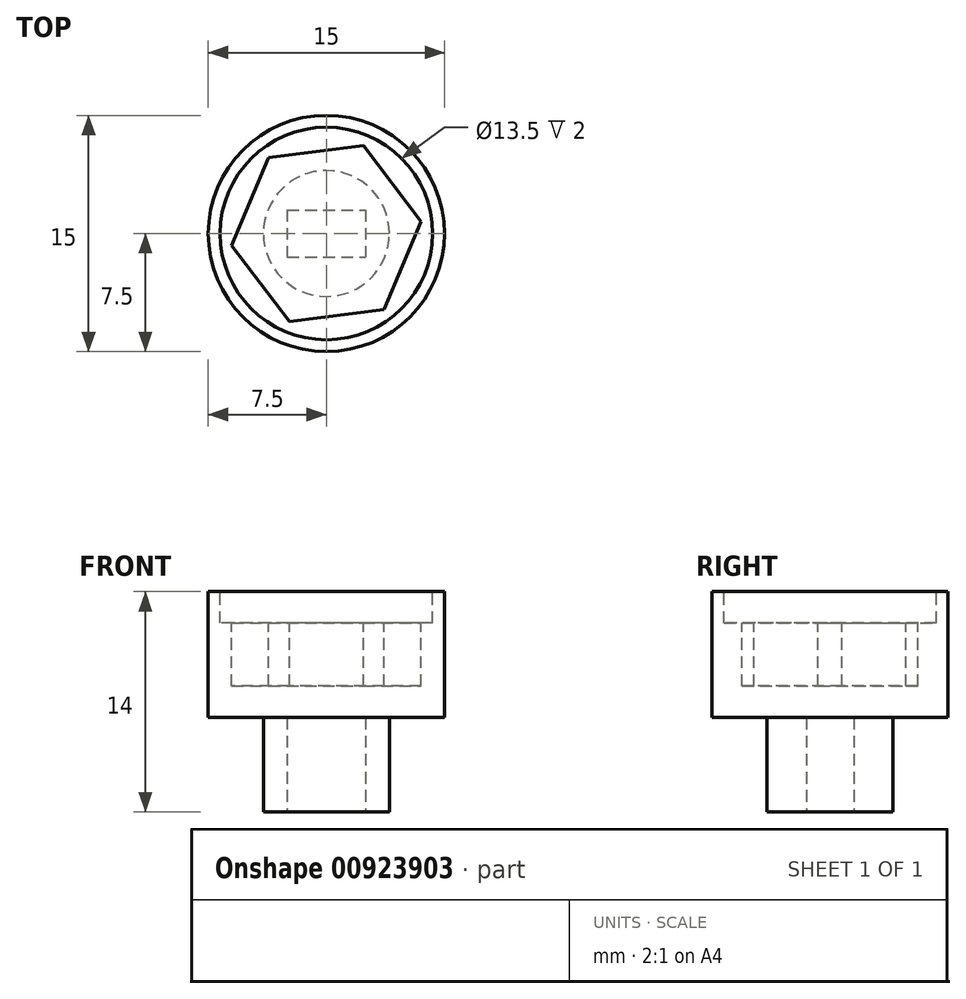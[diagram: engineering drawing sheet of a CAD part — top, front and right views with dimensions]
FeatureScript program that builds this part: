
annotation { "Feature Type Name" : "Feature", "Feature Type Description" : "" }
export const myFeature = defineFeature(function(context is Context, id is Id, definition is map)
    precondition{}
    {
        {
            var Q0;
            Q0=qCreatedBy(makeId("Top.planeOp"),FACE);
            var sketch = newSketch(context, id + "F0", { "sketchPlane" : qUnion([Q0])});
            skCircle(sketch, "E0", {"center": v(0, 0) * mm, "radius": 7.5 * mm});
            skSolve(sketch);
        }
        {
            var Q0;
            Q0 = qSketchRegion(id + "F0", true);
            extrude(context, id + "F1", {"entities" : qUnion([Q0]), "depth" : 8 * mm, "offsetDistance" : 25 * mm});
        }
        {
            var Q0;
            Q0=makeQuery(id+"F1.opExtrude","CAP_FACE",FACE,{"disambiguationData":[OSD([sQuery(id+"F0.wireOp",EDGE,"E0")])],"isStart":false});
            var sketch = newSketch(context, id + "F2", { "sketchPlane" : qUnion([Q0])});
            skCircle(sketch, "E1", {"center": v(0, 0) * mm, "radius": 6.75 * mm});
            skSolve(sketch);
        }
        {
            var Q0;
            Q0=makeQuery(id+"F2.imprint","IMPRINT",FACE,{"disambiguationData":[TD([[makeQuery(id+"F2.imprint","IMPRINT",EDGE,{"derivedFrom":sQuery(id+"F2.wireOp",EDGE,"E1")}),1.0]])]});
            extrude(context, id + "F3", {"entities" : qUnion([Q0]), "operationType" : NewBodyOperationType.REMOVE, "oppositeDirection" : true, "depth" : 2 * mm, "offsetDistance" : 25 * mm});
        }
        {
            var Q0;
            Q0=makeQuery(id+"F3.boolean.opBoolean","COPY",FACE,{"derivedFrom":makeQuery(id+"F3.opExtrude","CAP_FACE",FACE,{"disambiguationData":[OSD([sQuery(id+"F2.wireOp",EDGE,"E1")])],"isStart":false})});
            var sketch = newSketch(context, id + "F4", { "sketchPlane" : qUnion([Q0])});
            skCircle(sketch, "E2.cCircle", {"center": v(0, 0) * mm, "radius": 5.25 * mm, "construction": true});
            skLineSegment(sketch, "E2.0", {"start": v(2.34, 5.6) * mm, "end": v(6.01, 0.77) * mm});
            skLineSegment(sketch, "E2.1", {"start": v(6.01, 0.77) * mm, "end": v(3.67, -4.83) * mm});
            skLineSegment(sketch, "E2.2", {"start": v(3.67, -4.83) * mm, "end": v(-2.34, -5.6) * mm});
            skLineSegment(sketch, "E2.3", {"start": v(-2.34, -5.6) * mm, "end": v(-6.01, -0.77) * mm});
            skLineSegment(sketch, "E2.4", {"start": v(-6.01, -0.77) * mm, "end": v(-3.67, 4.83) * mm});
            skLineSegment(sketch, "E2.5", {"start": v(-3.67, 4.83) * mm, "end": v(2.34, 5.6) * mm});
            skPoint(sketch, "E2.0.midPoint", {"position": v(4.18, 3.18) * mm});
            skSolve(sketch);
        }
        {
            var Q0;
            Q0=makeQuery(id+"F4.imprint","IMPRINT",FACE,{"disambiguationData":[TD([[makeQuery(id+"F4.imprint","IMPRINT",EDGE,{"derivedFrom":sQuery(id+"F4.wireOp",EDGE,"E2.0")}),-1.0]])]});
            extrude(context, id + "F5", {"entities" : qUnion([Q0]), "operationType" : NewBodyOperationType.REMOVE, "oppositeDirection" : true, "depth" : 4 * mm, "offsetDistance" : 25 * mm});
        }
        {
            var Q0;
            Q0=makeQuery(id+"F1.opExtrude","CAP_FACE",FACE,{"disambiguationData":[OSD([sQuery(id+"F0.wireOp",EDGE,"E0")])],"isStart":true});
            var sketch = newSketch(context, id + "F6", { "sketchPlane" : qUnion([Q0])});
            skCircle(sketch, "E3", {"center": v(0, 0) * mm, "radius": 4 * mm});
            skSolve(sketch);
        }
        {
            var Q0;
            Q0=makeQuery(id+"F6.imprint","IMPRINT",FACE,{"disambiguationData":[TD([[makeQuery(id+"F6.imprint","IMPRINT",EDGE,{"derivedFrom":sQuery(id+"F6.wireOp",EDGE,"E3")}),1.0]])]});
            extrude(context, id + "F7", {"entities" : qUnion([Q0]), "operationType" : NewBodyOperationType.ADD, "depth" : 6 * mm, "offsetDistance" : 25 * mm});
        }
        {
            var Q0;
            Q0=makeQuery(id+"F7.opExtrude","CAP_FACE",FACE,{"disambiguationData":[OSD([sQuery(id+"F6.wireOp",EDGE,"E3")])],"isStart":false});
            var sketch = newSketch(context, id + "F8", { "sketchPlane" : qUnion([Q0])});
            skLineSegment(sketch, "E4.bottom", {"start": v(-2.5, -1.5) * mm, "end": v(2.5, -1.5) * mm});
            skLineSegment(sketch, "E4.top", {"start": v(-2.5, 1.5) * mm, "end": v(2.5, 1.5) * mm});
            skLineSegment(sketch, "E4.left", {"start": v(-2.5, -1.5) * mm, "end": v(-2.5, 1.5) * mm});
            skLineSegment(sketch, "E4.right", {"start": v(2.5, -1.5) * mm, "end": v(2.5, 1.5) * mm});
            skSolve(sketch);
        }
        {
            var Q0;
            Q0=makeQuery(id+"F8.imprint","IMPRINT",FACE,{"disambiguationData":[TD([[makeQuery(id+"F8.imprint","IMPRINT",EDGE,{"derivedFrom":sQuery(id+"F8.wireOp",EDGE,"E4.bottom")}),1.0]])]});
            extrude(context, id + "F9", {"entities" : qUnion([Q0]), "operationType" : NewBodyOperationType.REMOVE, "oppositeDirection" : true, "depth" : 6 * mm, "offsetDistance" : 25 * mm});
        }
    });
